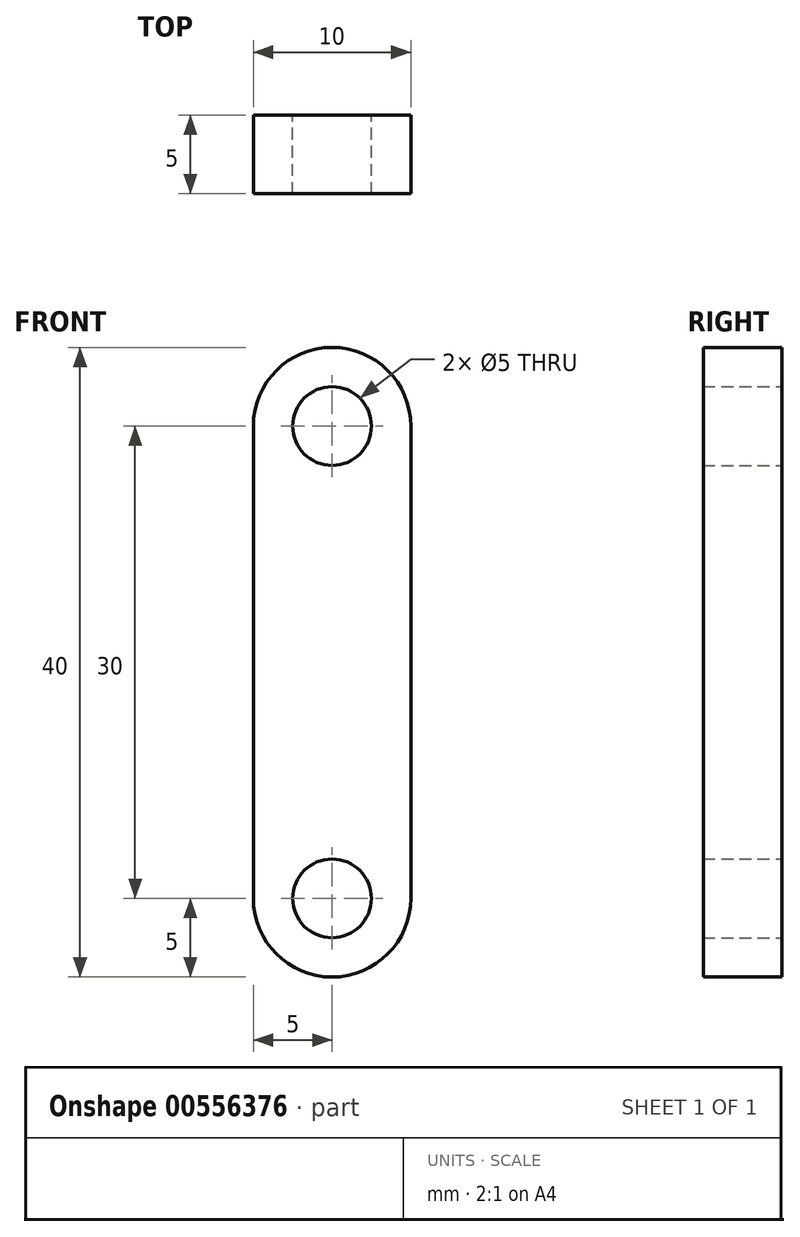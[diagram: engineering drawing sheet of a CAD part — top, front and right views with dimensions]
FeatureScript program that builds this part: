
annotation { "Feature Type Name" : "Feature", "Feature Type Description" : "" }
export const myFeature = defineFeature(function(context is Context, id is Id, definition is map)
    precondition{}
    {
        {
            var Q0;
            Q0=qCreatedBy(makeId("Front.planeOp"),FACE);
            var sketch = newSketch(context, id + "F0", { "sketchPlane" : qUnion([Q0])});
            skArc(sketch, "E0", {"start": v(-5, 0) * mm, "mid": v(0, -5) * mm, "end": v(5, 0) * mm});
            skArc(sketch, "E1", {"start": v(5, 30) * mm, "mid": v(0, 35) * mm, "end": v(-5, 30) * mm});
            skLineSegment(sketch, "E2", {"start": v(-5, 30) * mm, "end": v(-5, 0) * mm});
            skLineSegment(sketch, "E3", {"start": v(5, 30) * mm, "end": v(5, 0) * mm});
            skCircle(sketch, "E4", {"center": v(0, 30) * mm, "radius": 2.5 * mm});
            skCircle(sketch, "E5", {"center": v(0, 0) * mm, "radius": 2.5 * mm});
            skSolve(sketch);
        }
        {
            var Q0;
            Q0=makeQuery(id+"F0.imprint","IMPRINT",FACE,{"disambiguationData":[TD([[makeQuery(id+"F0.imprint","IMPRINT",EDGE,{"derivedFrom":sQuery(id+"F0.wireOp",EDGE,"E0")}),1.0]])]});
            extrude(context, id + "F1", {"entities" : qUnion([Q0]), "depth" : 5 * mm, "offsetDistance" : 25 * mm});
        }
    });
